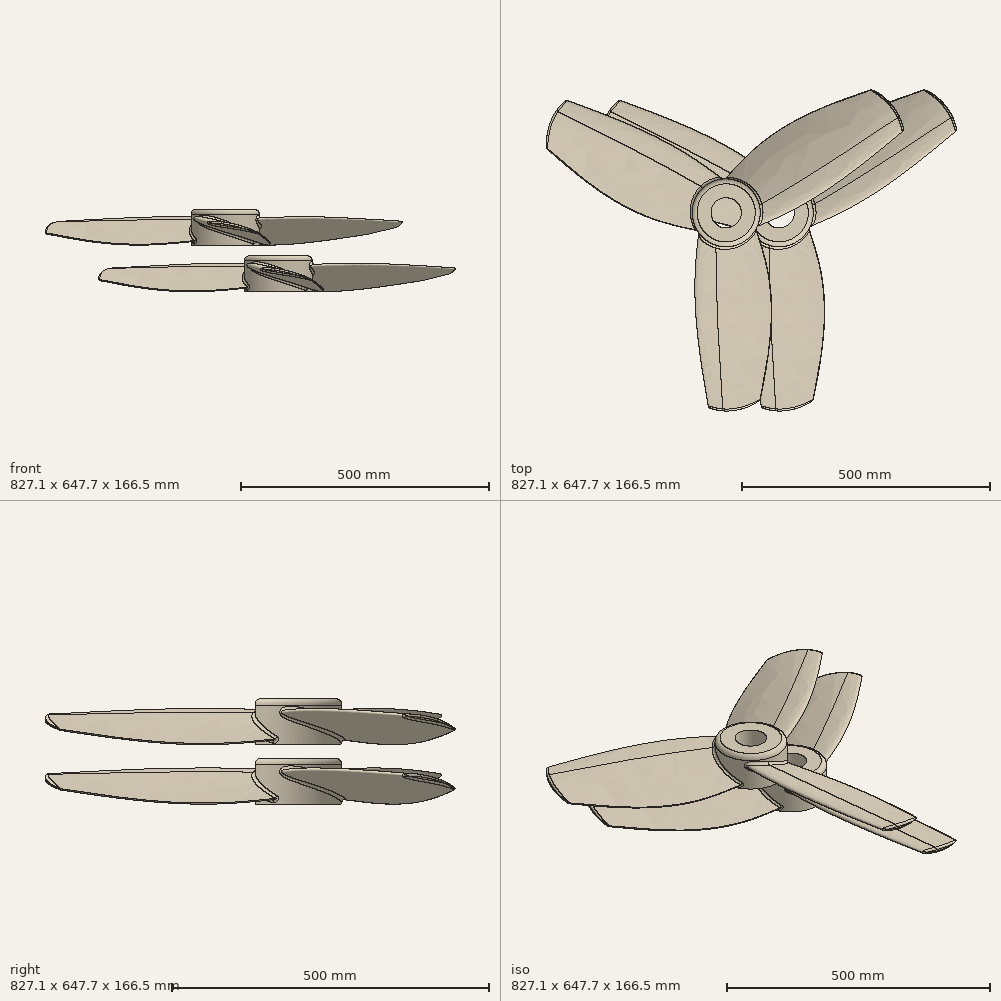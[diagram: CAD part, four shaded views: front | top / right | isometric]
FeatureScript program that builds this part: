
annotation { "Feature Type Name" : "Feature", "Feature Type Description" : "" }
export const myFeature = defineFeature(function(context is Context, id is Id, definition is map)
    precondition{}
    {
        {
            var Q0;
            Q0=qCreatedBy(makeId("Front.planeOp"),FACE);
            var sketch = newSketch(context, id + "F0", { "sketchPlane" : qUnion([Q0])});
            skLineSegment(sketch, "E0", {"start": v(-25.68, 10.16) * mm, "end": v(0, 0) * mm, "construction": true});
            skLineSegment(sketch, "E1", {"start": v(0, 0) * mm, "end": v(25.68, -10.16) * mm, "construction": true});
            skLineSegment(sketch, "E2", {"start": v(25.68, -10.16) * mm, "end": v(51.36, -20.31) * mm, "construction": true});
            skLineSegment(sketch, "E3", {"start": v(51.36, -20.31) * mm, "end": v(77.03, -30.47) * mm, "construction": true});
            skLineSegment(sketch, "E4", {"start": v(0, 0) * mm, "end": v(3.73, 9.44) * mm, "construction": true});
            skLineSegment(sketch, "E5", {"start": v(-25.68, 10.16) * mm, "end": v(-23.81, 14.88) * mm, "construction": true});
            skFitSpline(sketch, "E6", {"points": [v(-25.68, 10.16) * mm, v(3.73, 9.44) * mm, v(77.03, -30.47) * mm], "startDerivative": vector(15.03, 38) * mm, "endDerivative": vector(104.92, -93.69) * mm});
            skPoint(sketch, "E7", {"position": v(1.87, 4.72) * mm});
            skLineSegment(sketch, "E8", {"start": v(-23.81, 14.88) * mm, "end": v(1.87, 4.72) * mm, "construction": true});
            skLineSegment(sketch, "E9", {"start": v(0, 0) * mm, "end": v(-1.87, -4.72) * mm, "construction": true});
            skLineSegment(sketch, "E10", {"start": v(-25.68, 10.16) * mm, "end": v(-27.54, 5.44) * mm, "construction": true});
            skFitSpline(sketch, "E11", {"points": [v(-25.68, 10.16) * mm, v(-1.87, -4.72) * mm, v(77.03, -30.47) * mm], "startDerivative": vector(-15.23, -38.5) * mm, "endDerivative": vector(121.84, -48.19) * mm});
            skLineSegment(sketch, "E12", {"start": v(51.36, -20.31) * mm, "end": v(55.09, -10.87) * mm, "construction": true});
            skSolve(sketch);
        }
        {
            var Q0;
            Q0=qCreatedBy(makeId("Front.planeOp"),FACE);
            cPlane(context, id + "F1", {"entities" : qUnion([Q0]), "cplaneType" : CPlaneType.OFFSET, "offset" : 125 * mm, "width" : 150 * mm, "height" : 150 * mm});
        }
        {
            var Q0;
            Q0=qCreatedBy(id+"F1.planeOp",FACE);
            var sketch = newSketch(context, id + "F2", { "sketchPlane" : qUnion([Q0])});
            skLineSegment(sketch, "E13", {"start": v(-38.33, 14.06) * mm, "end": v(0, 0) * mm, "construction": true});
            skLineSegment(sketch, "E14", {"start": v(0, 0) * mm, "end": v(38.33, -14.06) * mm, "construction": true});
            skLineSegment(sketch, "E15", {"start": v(38.33, -14.06) * mm, "end": v(76.67, -28.12) * mm, "construction": true});
            skLineSegment(sketch, "E16", {"start": v(76.67, -28.12) * mm, "end": v(115, -42.17) * mm, "construction": true});
            skLineSegment(sketch, "E17", {"start": v(0, 0) * mm, "end": v(4.06, 11.06) * mm, "construction": true});
            skLineSegment(sketch, "E18", {"start": v(-38.33, 14.06) * mm, "end": v(-36.3, 19.59) * mm, "construction": true});
            skFitSpline(sketch, "E19", {"points": [v(-38.33, 14.06) * mm, v(4.06, 11.06) * mm, v(115, -42.17) * mm], "startDerivative": vector(16.44, 44.82) * mm, "endDerivative": vector(163.27, -119.63) * mm});
            skPoint(sketch, "E20", {"position": v(2.03, 5.53) * mm});
            skLineSegment(sketch, "E21", {"start": v(-36.3, 19.59) * mm, "end": v(2.03, 5.53) * mm, "construction": true});
            skLineSegment(sketch, "E22", {"start": v(0, 0) * mm, "end": v(-2.03, -5.53) * mm, "construction": true});
            skLineSegment(sketch, "E23", {"start": v(-38.33, 14.06) * mm, "end": v(-40.36, 8.53) * mm, "construction": true});
            skFitSpline(sketch, "E24", {"points": [v(-38.33, 14.06) * mm, v(-2.03, -5.53) * mm, v(115, -42.17) * mm], "startDerivative": vector(-16.57, -45.19) * mm, "endDerivative": vector(181.7, -66.64) * mm});
            skLineSegment(sketch, "E25", {"start": v(76.67, -28.12) * mm, "end": v(80.72, -17.06) * mm, "construction": true});
            skSolve(sketch);
        }
        {
            var Q0;
            Q0=qCreatedBy(makeId("Front.planeOp"),FACE);
            cPlane(context, id + "F3", {"entities" : qUnion([Q0]), "cplaneType" : CPlaneType.OFFSET, "offset" : 400 * mm, "width" : 150 * mm, "height" : 150 * mm});
        }
        {
            var Q0;
            Q0=qCreatedBy(id+"F3.planeOp",FACE);
            var sketch = newSketch(context, id + "F4", { "sketchPlane" : qUnion([Q0])});
            skLineSegment(sketch, "E26", {"start": v(-10.03, 5.14) * mm, "end": v(16.27, 0) * mm, "construction": true});
            skLineSegment(sketch, "E27", {"start": v(16.27, 0) * mm, "end": v(42.56, -5.14) * mm, "construction": true});
            skLineSegment(sketch, "E28", {"start": v(42.56, -5.14) * mm, "end": v(68.86, -10.28) * mm, "construction": true});
            skLineSegment(sketch, "E29", {"start": v(68.86, -10.28) * mm, "end": v(95.16, -15.42) * mm, "construction": true});
            skLineSegment(sketch, "E30", {"start": v(16.27, 0) * mm, "end": v(17.61, 6.9) * mm, "construction": true});
            skLineSegment(sketch, "E31", {"start": v(-10.03, 5.14) * mm, "end": v(-9.36, 8.59) * mm, "construction": true});
            skFitSpline(sketch, "E32", {"points": [v(-10.03, 5.14) * mm, v(17.61, 6.9) * mm, v(95.16, -15.42) * mm], "startDerivative": vector(5.47, 28.01) * mm, "endDerivative": vector(118.7, -57.28) * mm});
            skPoint(sketch, "E33", {"position": v(16.94, 3.45) * mm});
            skLineSegment(sketch, "E34", {"start": v(-9.36, 8.59) * mm, "end": v(16.94, 3.45) * mm, "construction": true});
            skLineSegment(sketch, "E35", {"start": v(16.27, 0) * mm, "end": v(15.6, -3.45) * mm, "construction": true});
            skLineSegment(sketch, "E36", {"start": v(-10.03, 5.14) * mm, "end": v(-10.7, 1.7) * mm, "construction": true});
            skFitSpline(sketch, "E37", {"points": [v(-10.03, 5.14) * mm, v(15.6, -3.45) * mm, v(95.16, -15.42) * mm], "startDerivative": vector(-5.51, -28.2) * mm, "endDerivative": vector(124.61, -24.36) * mm});
            skLineSegment(sketch, "E38", {"start": v(68.86, -10.28) * mm, "end": v(70.2, -3.38) * mm, "construction": true});
            skSolve(sketch);
        }
        {
            var Q0;
            Q0=qSketchRegion(id+"F0",true);
            var Q1;
            Q1=qSketchRegion(id+"F2",true);
            var Q2;
            Q2=qSketchRegion(id+"F4",true);
            var Q3;
            Q3=sQuery(id+"F0.wireOp",VERTEX,"E6.1.internal");
            var Q4;
            Q4=sQuery(id+"F2.wireOp",VERTEX,"E19.1.internal");
            var Q5;
            Q5=sQuery(id+"F4.wireOp",VERTEX,"E30.end");
            loft(context, id + "F5", {"sheetProfilesArray" : [{ "sheetProfileEntities" : qUnion([Q0]) }, { "sheetProfileEntities" : qUnion([Q1]) }, { "sheetProfileEntities" : qUnion([Q2]) }], "matchConnections" : true, "connections" : [{ "connectionEntities" : qUnion([Q3, Q4, Q5]), "connectionEdgeQueries" : qUnion([]), "connectionEdgeParameters" : [] }]});
        }
        {
            var Q0;
            Q0=qCreatedBy(makeId("Top.planeOp"),FACE);
            var sketch = newSketch(context, id + "F6", { "sketchPlane" : qUnion([Q0])});
            skFitSpline(sketch, "E39", {"points": [v(-55.98, -360.47) * mm, v(39.38, -398.87) * mm, v(142.8, -333.19) * mm], "startDerivative": vector(111.22, -150.8) * mm, "endDerivative": vector(54.24, 145.78) * mm});
            skLineSegment(sketch, "E40", {"start": v(-55.98, -360.47) * mm, "end": v(-55.98, -458.75) * mm});
            skLineSegment(sketch, "E41", {"start": v(142.8, -333.19) * mm, "end": v(142.8, -458.75) * mm});
            skLineSegment(sketch, "E42", {"start": v(142.8, -458.75) * mm, "end": v(-55.98, -458.75) * mm});
            skSolve(sketch);
        }
        {
            var Q0;
            Q0=qSketchRegion(id+"F6",true);
            extrude(context, id + "F7", {"entities" : qUnion([Q0]), "operationType" : NewBodyOperationType.REMOVE, "endBound" : BoundingType.SYMMETRIC, "oppositeDirection" : true, "depth" : 40.17 * mm});
        }
        {
            var Q0;
            Q0=makeQuery(id+"F5.opLoft","SWEPT_EDGE",EDGE,{"disambiguationData":[OSD([sQuery(id+"F2.wireOp",EDGE,"E19"),sQuery(id+"F2.wireOp",EDGE,"E24"),sQuery(id+"F4.wireOp",EDGE,"E32"),sQuery(id+"F4.wireOp",EDGE,"E37")])]});
            fillet(context, id + "F8", {"entities" : qUnion([Q0]), "radius" : 1 * mm, "tangentPropagation" : true, "allowEdgeOverflow" : false});
        }
        {
            var Q0;
            Q0=makeQuery(id+"F7.boolean.opBoolean","COPY",FACE,{"derivedFrom":makeQuery(id+"F7.opExtrude","SWEPT_FACE",FACE,{"disambiguationData":[OSD([sQuery(id+"F6.wireOp",EDGE,"E39")])]})});
            fillet(context, id + "F9", {"entities" : qUnion([Q0]), "radius" : 4 * mm, "tangentPropagation" : true, "allowEdgeOverflow" : false});
        }
        {
            var Q0;
            Q0=qCreatedBy(makeId("Top.planeOp"),FACE);
            var sketch = newSketch(context, id + "F10", { "sketchPlane" : qUnion([Q0])});
            skCircle(sketch, "E43", {"center": v(24.35, 0) * mm, "radius": 68.6 * mm});
            skSolve(sketch);
        }
        {
            var Q0;
            Q0=qSketchRegion(id+"F10",true);
            extrude(context, id + "F11", {"entities" : qUnion([Q0]), "depth" : 32.31 * mm, "hasSecondDirection" : true, "secondDirectionOppositeDirection" : true, "secondDirectionDepth" : 40 * mm});
        }
        {
            var Q0;
            Q0=makeQuery(id+"F5.opLoft","SWEPT_BODY",BODY,{"disambiguationData":[OSD([makeQuery(id+"F0.imprint","IMPRINT",FACE,{"disambiguationData":[TD([[makeQuery(id+"F0.imprint","IMPRINT",EDGE,{"derivedFrom":sQuery(id+"F0.wireOp",EDGE,"E6")}),-1.0]])]}),sQuery(id+"F2.wireOp",EDGE,"E24"),makeQuery(id+"F4.imprint","IMPRINT",FACE,{"disambiguationData":[TD([[makeQuery(id+"F4.imprint","IMPRINT",EDGE,{"derivedFrom":sQuery(id+"F4.wireOp",EDGE,"E32")}),-1.0]])]})])]});
            var Q1;
            Q1=makeQuery(id+"F11.opExtrude","SWEPT_FACE",FACE,{"disambiguationData":[OSD([sQuery(id+"F10.wireOp",EDGE,"E43")])]});
            circularPattern(context, id + "F12", {"entities" : qUnion([Q0]), "axis" : qUnion([Q1]), "angle" : 360 * degree, "instanceCount" : 3, "equalSpace" : true});
        }
        {
            var Q0;
            Q0=makeQuery(id+"F12.opPattern","COPY",BODY,{"derivedFrom":makeQuery(id+"F5.opLoft","SWEPT_BODY",BODY,{"disambiguationData":[OSD([makeQuery(id+"F0.imprint","IMPRINT",FACE,{"disambiguationData":[TD([[makeQuery(id+"F0.imprint","IMPRINT",EDGE,{"derivedFrom":sQuery(id+"F0.wireOp",EDGE,"E6")}),-1.0]])]}),sQuery(id+"F2.wireOp",EDGE,"E24"),makeQuery(id+"F4.imprint","IMPRINT",FACE,{"disambiguationData":[TD([[makeQuery(id+"F4.imprint","IMPRINT",EDGE,{"derivedFrom":sQuery(id+"F4.wireOp",EDGE,"E32")}),-1.0]])]})])]}),"instanceName":"2"});
            var Q1;
            Q1=makeQuery(id+"F5.opLoft","SWEPT_BODY",BODY,{"disambiguationData":[OSD([makeQuery(id+"F0.imprint","IMPRINT",FACE,{"disambiguationData":[TD([[makeQuery(id+"F0.imprint","IMPRINT",EDGE,{"derivedFrom":sQuery(id+"F0.wireOp",EDGE,"E6")}),-1.0]])]}),sQuery(id+"F2.wireOp",EDGE,"E24"),makeQuery(id+"F4.imprint","IMPRINT",FACE,{"disambiguationData":[TD([[makeQuery(id+"F4.imprint","IMPRINT",EDGE,{"derivedFrom":sQuery(id+"F4.wireOp",EDGE,"E32")}),-1.0]])]})])]});
            var Q2;
            Q2=makeQuery(id+"F11.opExtrude","SWEPT_BODY",BODY,{"disambiguationData":[OSD([sQuery(id+"F10.wireOp",EDGE,"E43")])]});
            var Q3;
            Q3=makeQuery(id+"F12.opPattern","COPY",BODY,{"derivedFrom":makeQuery(id+"F5.opLoft","SWEPT_BODY",BODY,{"disambiguationData":[OSD([makeQuery(id+"F0.imprint","IMPRINT",FACE,{"disambiguationData":[TD([[makeQuery(id+"F0.imprint","IMPRINT",EDGE,{"derivedFrom":sQuery(id+"F0.wireOp",EDGE,"E6")}),-1.0]])]}),sQuery(id+"F2.wireOp",EDGE,"E24"),makeQuery(id+"F4.imprint","IMPRINT",FACE,{"disambiguationData":[TD([[makeQuery(id+"F4.imprint","IMPRINT",EDGE,{"derivedFrom":sQuery(id+"F4.wireOp",EDGE,"E32")}),-1.0]])]})])]}),"instanceName":"1"});
            var Q4;
            Q4=makeQuery(id+"F12.opPattern","COPY",BODY,{"derivedFrom":makeQuery(id+"F5.opLoft","SWEPT_BODY",BODY,{"disambiguationData":[OSD([makeQuery(id+"F0.imprint","IMPRINT",FACE,{"disambiguationData":[TD([[makeQuery(id+"F0.imprint","IMPRINT",EDGE,{"derivedFrom":sQuery(id+"F0.wireOp",EDGE,"E6")}),-1.0]])]}),sQuery(id+"F2.wireOp",EDGE,"E24"),makeQuery(id+"F4.imprint","IMPRINT",FACE,{"disambiguationData":[TD([[makeQuery(id+"F4.imprint","IMPRINT",EDGE,{"derivedFrom":sQuery(id+"F4.wireOp",EDGE,"E32")}),-1.0]])]})])]}),"instanceName":"4"});
            var Q5;
            Q5=makeQuery(id+"F12.opPattern","COPY",BODY,{"derivedFrom":makeQuery(id+"F5.opLoft","SWEPT_BODY",BODY,{"disambiguationData":[OSD([makeQuery(id+"F0.imprint","IMPRINT",FACE,{"disambiguationData":[TD([[makeQuery(id+"F0.imprint","IMPRINT",EDGE,{"derivedFrom":sQuery(id+"F0.wireOp",EDGE,"E6")}),-1.0]])]}),sQuery(id+"F2.wireOp",EDGE,"E24"),makeQuery(id+"F4.imprint","IMPRINT",FACE,{"disambiguationData":[TD([[makeQuery(id+"F4.imprint","IMPRINT",EDGE,{"derivedFrom":sQuery(id+"F4.wireOp",EDGE,"E32")}),-1.0]])]})])]}),"instanceName":"3"});
            booleanBodies(context, id + "F13", {"operationType" : BooleanOperationType.UNION, "tools" : qUnion([Q0, Q1, Q2, Q3, Q4, Q5])});
        }
        {
            var Q0;
            Q0=makeQuery(id+"F11.opExtrude","CAP_FACE",FACE,{"disambiguationData":[OSD([sQuery(id+"F10.wireOp",EDGE,"E43")])],"isStart":false});
            var sketch = newSketch(context, id + "F14", { "sketchPlane" : qUnion([Q0])});
            skCircle(sketch, "E44", {"center": v(24.35, 0) * mm, "radius": 30.45 * mm});
            skSolve(sketch);
        }
        {
            var Q0;
            Q0=qSketchRegion(id+"F14",true);
            extrude(context, id + "F15", {"entities" : qUnion([Q0]), "operationType" : NewBodyOperationType.REMOVE, "endBound" : BoundingType.THROUGH_ALL, "oppositeDirection" : true, "depth" : 25 * mm});
        }
        {
            var Q0;
            {var subQ0=sQuery(id+"F0.wireOp",VERTEX,"E6.1.internal");var subQ1=sQuery(id+"F0.wireOp",EDGE,"E6");var subQ2=sQuery(id+"F0.wireOp",EDGE,"E11");var subQ3=sQuery(id+"F2.wireOp",VERTEX,"E19.1.internal");var subQ4=sQuery(id+"F2.wireOp",EDGE,"E19");var subQ5=sQuery(id+"F2.wireOp",EDGE,"E24");Q0=makeQuery(id+"F13.opBoolean","INTERSECT",EDGE,{"derivedFrom":[makeQuery(id+"F11.opExtrude","SWEPT_FACE",FACE,{"disambiguationData":[OSD([sQuery(id+"F10.wireOp",EDGE,"E43")])]}),makeQuery(id+"F12.opPattern","COPY",FACE,{"derivedFrom":makeQuery(id+"F5.opLoft","SWEPT_FACE",FACE,{"disambiguationData":[OSD([subQ0,subQ1,subQ2,subQ3,subQ4,subQ5]),TDD([subQ0,makeQuery(id+"F0.imprint","INTERSECT",VERTEX,{"disambiguationData":[OD(0.0)],"derivedFrom":[subQ1,subQ2]}),makeQuery(id+"F0.imprint","IMPRINT",EDGE,{"derivedFrom":subQ1}),subQ3,makeQuery(id+"F2.imprint","INTERSECT",VERTEX,{"disambiguationData":[OD(0.0)],"derivedFrom":[subQ4,subQ5]}),makeQuery(id+"F2.imprint","IMPRINT",EDGE,{"derivedFrom":subQ4})])]}),"instanceName":"2"})]});}
            var Q1;
            {var subQ0=sQuery(id+"F0.wireOp",VERTEX,"E6.1.internal");var subQ1=sQuery(id+"F0.wireOp",EDGE,"E6");var subQ2=sQuery(id+"F0.wireOp",EDGE,"E11");var subQ3=sQuery(id+"F2.wireOp",VERTEX,"E19.1.internal");var subQ4=sQuery(id+"F2.wireOp",EDGE,"E19");var subQ5=sQuery(id+"F2.wireOp",EDGE,"E24");Q1=makeQuery(id+"F13.opBoolean","INTERSECT",EDGE,{"derivedFrom":[makeQuery(id+"F5.opLoft","SWEPT_FACE",FACE,{"disambiguationData":[OSD([subQ0,subQ1,subQ2,subQ3,subQ4,subQ5]),TDD([subQ0,makeQuery(id+"F0.imprint","INTERSECT",VERTEX,{"disambiguationData":[OD(1.0)],"derivedFrom":[subQ1,subQ2]}),makeQuery(id+"F0.imprint","IMPRINT",EDGE,{"derivedFrom":subQ1}),subQ3,makeQuery(id+"F2.imprint","INTERSECT",VERTEX,{"disambiguationData":[OD(1.0)],"derivedFrom":[subQ4,subQ5]}),makeQuery(id+"F2.imprint","IMPRINT",EDGE,{"derivedFrom":subQ4})])]}),makeQuery(id+"F11.opExtrude","SWEPT_FACE",FACE,{"disambiguationData":[OSD([sQuery(id+"F10.wireOp",EDGE,"E43")])]})]});}
            var Q2;
            {var subQ0=sQuery(id+"F0.wireOp",VERTEX,"E6.1.internal");var subQ1=sQuery(id+"F0.wireOp",EDGE,"E6");var subQ2=sQuery(id+"F0.wireOp",EDGE,"E11");var subQ3=sQuery(id+"F2.wireOp",VERTEX,"E19.1.internal");var subQ4=sQuery(id+"F2.wireOp",EDGE,"E19");var subQ5=sQuery(id+"F2.wireOp",EDGE,"E24");Q2=makeQuery(id+"F13.opBoolean","INTERSECT",EDGE,{"derivedFrom":[makeQuery(id+"F11.opExtrude","SWEPT_FACE",FACE,{"disambiguationData":[OSD([sQuery(id+"F10.wireOp",EDGE,"E43")])]}),makeQuery(id+"F12.opPattern","COPY",FACE,{"derivedFrom":makeQuery(id+"F5.opLoft","SWEPT_FACE",FACE,{"disambiguationData":[OSD([subQ0,subQ1,subQ2,subQ3,subQ4,subQ5]),TDD([subQ0,makeQuery(id+"F0.imprint","INTERSECT",VERTEX,{"disambiguationData":[OD(1.0)],"derivedFrom":[subQ1,subQ2]}),makeQuery(id+"F0.imprint","IMPRINT",EDGE,{"derivedFrom":subQ1}),subQ3,makeQuery(id+"F2.imprint","INTERSECT",VERTEX,{"disambiguationData":[OD(1.0)],"derivedFrom":[subQ4,subQ5]}),makeQuery(id+"F2.imprint","IMPRINT",EDGE,{"derivedFrom":subQ4})])]}),"instanceName":"1"})]});}
            var Q3;
            {var subQ0=sQuery(id+"F0.wireOp",VERTEX,"E6.1.internal");var subQ1=sQuery(id+"F0.wireOp",EDGE,"E6");var subQ2=sQuery(id+"F0.wireOp",EDGE,"E11");var subQ3=sQuery(id+"F2.wireOp",VERTEX,"E19.1.internal");var subQ4=sQuery(id+"F2.wireOp",EDGE,"E19");var subQ5=sQuery(id+"F2.wireOp",EDGE,"E24");Q3=makeQuery(id+"F13.opBoolean","INTERSECT",EDGE,{"derivedFrom":[makeQuery(id+"F11.opExtrude","SWEPT_FACE",FACE,{"disambiguationData":[OSD([sQuery(id+"F10.wireOp",EDGE,"E43")])]}),makeQuery(id+"F12.opPattern","COPY",FACE,{"derivedFrom":makeQuery(id+"F5.opLoft","SWEPT_FACE",FACE,{"disambiguationData":[OSD([subQ0,subQ1,subQ2,subQ3,subQ4,subQ5]),TDD([subQ0,makeQuery(id+"F0.imprint","INTERSECT",VERTEX,{"disambiguationData":[OD(1.0)],"derivedFrom":[subQ1,subQ2]}),makeQuery(id+"F0.imprint","IMPRINT",EDGE,{"derivedFrom":subQ1}),subQ3,makeQuery(id+"F2.imprint","INTERSECT",VERTEX,{"disambiguationData":[OD(1.0)],"derivedFrom":[subQ4,subQ5]}),makeQuery(id+"F2.imprint","IMPRINT",EDGE,{"derivedFrom":subQ4})])]}),"instanceName":"4"})]});}
            var Q4;
            {var subQ0=sQuery(id+"F0.wireOp",VERTEX,"E6.1.internal");var subQ1=sQuery(id+"F0.wireOp",EDGE,"E6");var subQ2=sQuery(id+"F0.wireOp",EDGE,"E11");var subQ3=sQuery(id+"F2.wireOp",VERTEX,"E19.1.internal");var subQ4=sQuery(id+"F2.wireOp",EDGE,"E19");var subQ5=sQuery(id+"F2.wireOp",EDGE,"E24");Q4=makeQuery(id+"F13.opBoolean","INTERSECT",EDGE,{"derivedFrom":[makeQuery(id+"F11.opExtrude","SWEPT_FACE",FACE,{"disambiguationData":[OSD([sQuery(id+"F10.wireOp",EDGE,"E43")])]}),makeQuery(id+"F12.opPattern","COPY",FACE,{"derivedFrom":makeQuery(id+"F5.opLoft","SWEPT_FACE",FACE,{"disambiguationData":[OSD([subQ0,subQ1,subQ2,subQ3,subQ4,subQ5]),TDD([subQ0,makeQuery(id+"F0.imprint","INTERSECT",VERTEX,{"disambiguationData":[OD(0.0)],"derivedFrom":[subQ1,subQ2]}),makeQuery(id+"F0.imprint","IMPRINT",EDGE,{"derivedFrom":subQ1}),subQ3,makeQuery(id+"F2.imprint","INTERSECT",VERTEX,{"disambiguationData":[OD(0.0)],"derivedFrom":[subQ4,subQ5]}),makeQuery(id+"F2.imprint","IMPRINT",EDGE,{"derivedFrom":subQ4})])]}),"instanceName":"3"})]});}
            fillet(context, id + "F16", {"entities" : qUnion([Q0, Q1, Q2, Q3, Q4]), "radius" : 5 * mm, "tangentPropagation" : true, "allowEdgeOverflow" : false});
        }
        {
            var Q0;
            Q0=makeQuery(id+"F11.opExtrude","CAP_EDGE",EDGE,{"disambiguationData":[OSD([sQuery(id+"F10.wireOp",EDGE,"E43")])],"isStart":false});
            fillet(context, id + "F17", {"entities" : qUnion([Q0]), "radius" : 10 * mm, "tangentPropagation" : true, "allowEdgeOverflow" : false});
        }
        {
            var Q0;
            Q0=makeQuery(id+"F12.opPattern","COPY",BODY,{"derivedFrom":makeQuery(id+"F5.opLoft","SWEPT_BODY",BODY,{"disambiguationData":[OSD([makeQuery(id+"F0.imprint","IMPRINT",FACE,{"disambiguationData":[TD([[makeQuery(id+"F0.imprint","IMPRINT",EDGE,{"derivedFrom":sQuery(id+"F0.wireOp",EDGE,"E6")}),-1.0]])]}),sQuery(id+"F2.wireOp",EDGE,"E19"),makeQuery(id+"F4.imprint","IMPRINT",FACE,{"disambiguationData":[TD([[makeQuery(id+"F4.imprint","IMPRINT",EDGE,{"derivedFrom":sQuery(id+"F4.wireOp",EDGE,"E32")}),-1.0]])]})])]}),"instanceName":"2"});
            transform(context, id + "F18", {"entities" : qUnion([Q0]), "transformType" : TransformType.TRANSLATION_3D, "dx" : -105 * mm, "dy" : 142 * mm, "dz" : 0 * mm, "makeCopy" : false});
        }
        {
            var Q0;
            Q0=makeQuery(id+"F12.opPattern","COPY",BODY,{"derivedFrom":makeQuery(id+"F5.opLoft","SWEPT_BODY",BODY,{"disambiguationData":[OSD([makeQuery(id+"F0.imprint","IMPRINT",FACE,{"disambiguationData":[TD([[makeQuery(id+"F0.imprint","IMPRINT",EDGE,{"derivedFrom":sQuery(id+"F0.wireOp",EDGE,"E6")}),-1.0]])]}),sQuery(id+"F2.wireOp",EDGE,"E19"),makeQuery(id+"F4.imprint","IMPRINT",FACE,{"disambiguationData":[TD([[makeQuery(id+"F4.imprint","IMPRINT",EDGE,{"derivedFrom":sQuery(id+"F4.wireOp",EDGE,"E32")}),-1.0]])]})])]}),"instanceName":"2"});
            transform(context, id + "F19", {"entities" : qUnion([Q0]), "transformType" : TransformType.TRANSLATION_3D, "dx" : -107 * mm, "dy" : 0 * mm, "dz" : 94 * mm, "makeCopy" : true});
        }
    });
